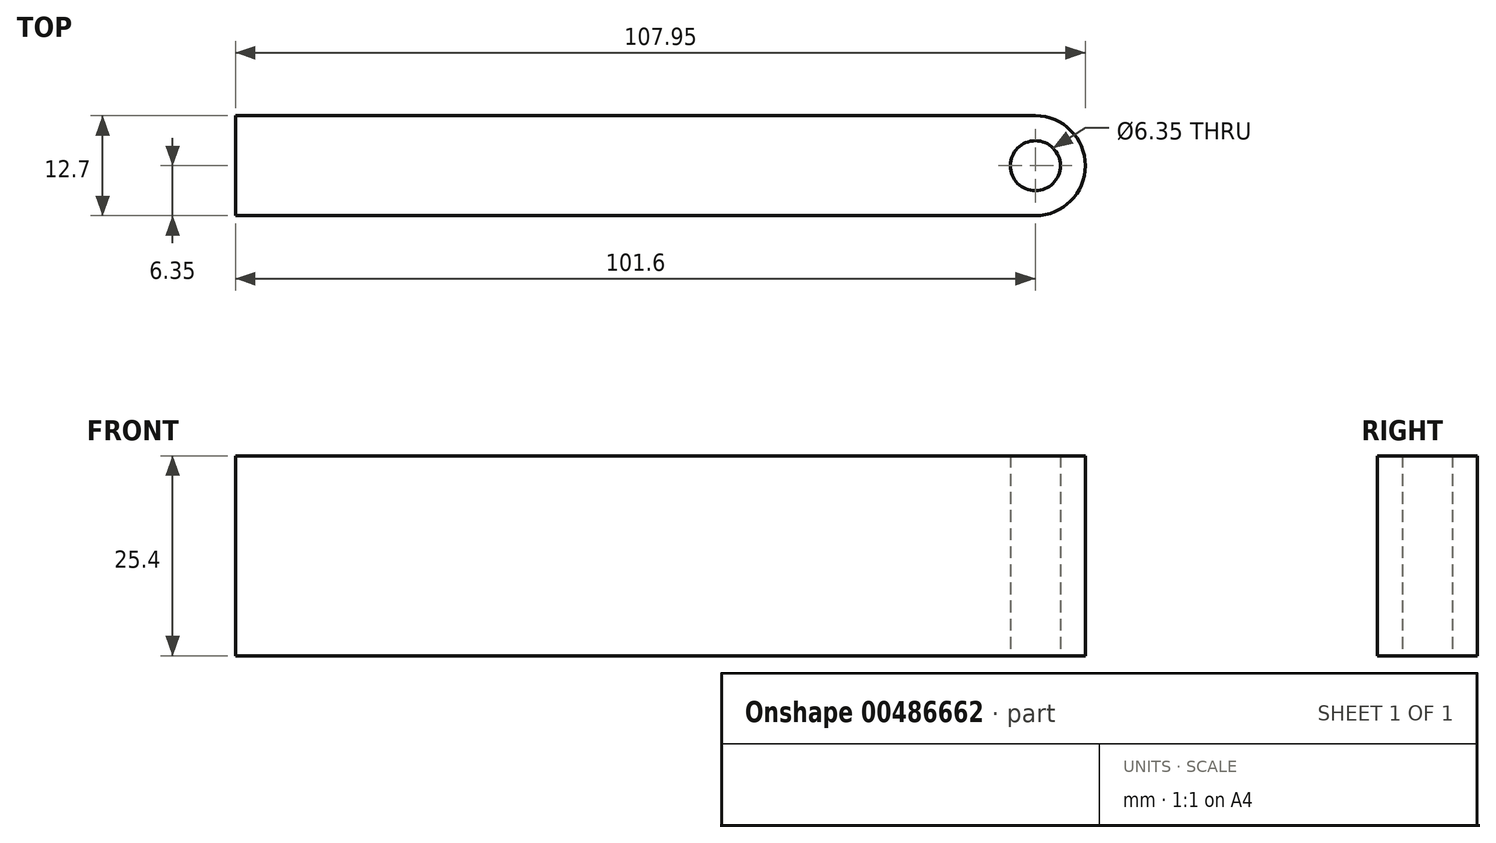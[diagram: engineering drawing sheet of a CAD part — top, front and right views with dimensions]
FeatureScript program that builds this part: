
annotation { "Feature Type Name" : "Feature", "Feature Type Description" : "" }
export const myFeature = defineFeature(function(context is Context, id is Id, definition is map)
    precondition{}
    {
        {
            var Q0;
            Q0=qCreatedBy(makeId("Top.planeOp"),FACE);
            var sketch = newSketch(context, id + "F0", { "sketchPlane" : qUnion([Q0])});
            skLineSegment(sketch, "E0.bottom", {"start": v(-50.8, 6.35) * mm, "end": v(50.8, 6.35) * mm});
            skLineSegment(sketch, "E0.top", {"start": v(-50.8, -6.35) * mm, "end": v(50.8, -6.35) * mm});
            skLineSegment(sketch, "E0.left", {"start": v(-50.8, 6.35) * mm, "end": v(-50.8, -6.35) * mm});
            skLineSegment(sketch, "E0.right", {"start": v(50.8, 6.35) * mm, "end": v(50.8, -6.35) * mm});
            skPoint(sketch, "E0.middle", {"position": v(0, 0) * mm});
            skArc(sketch, "E1", {"start": v(50.8, -6.35) * mm, "mid": v(57.15, 0) * mm, "end": v(50.8, 6.35) * mm});
            skCircle(sketch, "E2", {"center": v(50.8, 0) * mm, "radius": 3.18 * mm});
            skSolve(sketch);
        }
        {
            var Q0;
            Q0 = qSketchRegion(id + "F0", true);
            extrude(context, id + "F1", {"entities" : qUnion([Q0]), "depth" : 25.4 * mm, "offsetDistance" : 25.4 * mm});
        }
    });
